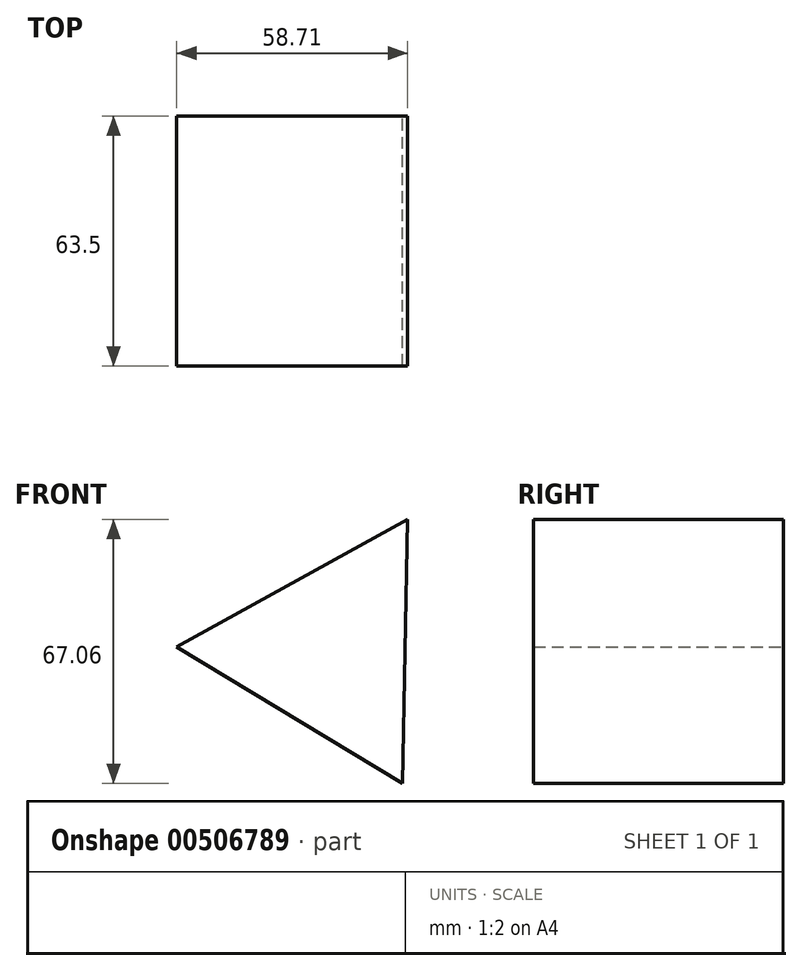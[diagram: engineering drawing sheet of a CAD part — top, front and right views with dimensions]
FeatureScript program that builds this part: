
annotation { "Feature Type Name" : "Feature", "Feature Type Description" : "" }
export const myFeature = defineFeature(function(context is Context, id is Id, definition is map)
    precondition{}
    {
        {
            var Q0;
            Q0=qCreatedBy(makeId("Front.planeOp"),FACE);
            var sketch = newSketch(context, id + "F0", { "sketchPlane" : qUnion([Q0])});
            skCircle(sketch, "E0.cCircle", {"center": v(-30.94, 44.54) * mm, "radius": 38.72 * mm, "construction": true});
            skLineSegment(sketch, "E0.0", {"start": v(-12.22, 10.64) * mm, "end": v(-69.66, 45.27) * mm});
            skLineSegment(sketch, "E0.1", {"start": v(-69.66, 45.27) * mm, "end": v(-10.95, 77.7) * mm});
            skLineSegment(sketch, "E0.2", {"start": v(-10.95, 77.7) * mm, "end": v(-12.22, 10.64) * mm});
            skSolve(sketch);
        }
        {
            var Q0;
            Q0 = qSketchRegion(id + "F0", true);
            extrude(context, id + "F1", {"entities" : qUnion([Q0]), "depth" : 63.5 * mm});
        }
    });
